# Revit family: Pico-03-Layout-Teknion-R2020
name_source: partatom
category: Furniture Systems
units: mm (PartAtom-declared; Revit-internal decimal feet)

## family parameters
Always vertical = Yes
Cut with Voids When Loaded = No
OmniClass Number = 23.40.70.14.64.21
OmniClass Title = Systems Furniture
Part Type = Normal
Room Calculation Point = No
Round Connector Dimension = Use Diameter
Shared = Yes
Work Plane-Based = No

## types (1)
- Pico 03
    Assembly Code = E2020200
    Default Elevation = 0' - 0"
    Description = 12'-3" x 8'-6" Overall
    Manufacturer = Studio TK
    Model = Pico 03
    Product Line = Pico
    Product Page URL = https://www.studiotk.com
    Series = Pico
    Sustainability Data = https://assets.teknion.com
    URL = https://www.studiotk.com
    Unit Weight URL = http://www.teknion.com
    Warranty = https://d2r72yk5wmppdj.cloudfront.net

## geometry (parser evidence)
native form markers: Blend x1, Sweep x11
no freeform markers — native parametric forms only
